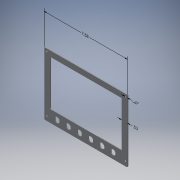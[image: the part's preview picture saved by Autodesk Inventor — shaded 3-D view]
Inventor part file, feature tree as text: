
AUTODESK INVENTOR PART (.ipt)
format: ipt  version: 2019 (Build 230136000, 136)  size: 230,400 bytes
history: native  units: in
note: dims shown in document units (in); Inventor stores cm internally (conversion verified against a paired STEP export)
features: other x4, direct_edit x3, move_body x3, extrude x2, sketch x2, imported_body x1
ambient origin geometry x8: Origin, YZ Plane, XZ Plane, XY Plane, X Axis, Y Axis, Z Axis, Center Point
bodies: Solid1 (feature_tree)
feature tree (15):
  other  "Annotations"
  direct_edit  "Direct Edit1"
  direct_edit  "Direct Edit2"
  extrude  "Extrusion1"  TaperAngle=0.0deg  [1 undecoded]
  extrude  "Extrusion2"  Depth=7.5772in
  direct_edit  "Direct Edit3"
  sketch  "Sketch1"  dims[d0=0.0in d1=0.0in d2=0.5906in d3=0.0in d4=-0.3937in d5=0.0in]
  sketch  "Sketch3"  dims[d6=0.4291in d7=0.2382in d8=0.2382in d9=2.3622in d11=1.0171in d12=0.3937in d14=0.3937in d16=0.5085in d17=0.5085in d18=6.1024in d19=0.3937in d20=0.0in d21=0.9843in d22=0.3937in d23=0.0in d27=0.0in d28=0.0in d29=0.53in d24=0.1329in d25=0.1168in d26=0.5315in d30=0.0129in d31=-0.0401in d32=0.2165in d36=0.0969in d37=0.3125in d38=7.5772in]
  imported_body  "Base1"
  move_body  "Move1"
  move_body  "Move2"
  move_body  "Move3"
  other  "Linear Dimension 1"
  other  "Linear Dimension 2"
  other  "Linear Dimension 3"
note: 1 required parameter value undecoded (feature->parameter linkage not recoverable at this tier; creation-order binding heuristic only, values carry confidence <= 0.55)
